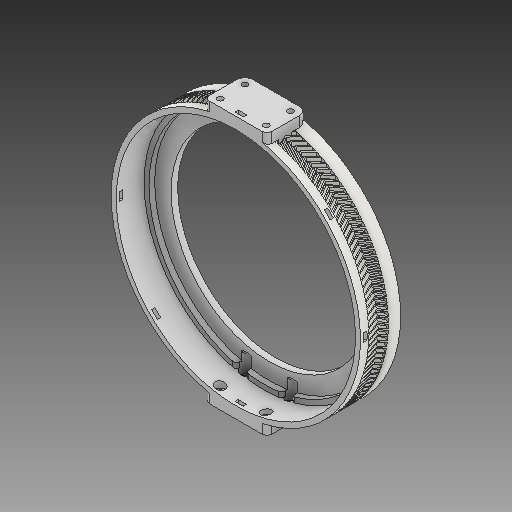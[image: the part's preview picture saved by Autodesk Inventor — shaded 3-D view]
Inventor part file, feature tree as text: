
AUTODESK INVENTOR PART (.ipt)
format: ipt  version: 2020 (Build 240168000, 168)  size: 2,971,648 bytes
history: native  units: in
note: dims shown in document units (in); Inventor stores cm internally (conversion verified against a paired STEP export)
features: other x5, extrude x5, sketch x5, plane x3, fillet x2, mirror x1
ambient origin geometry x8: Origin, YZ Plane, XZ Plane, XY Plane, X Axis, Y Axis, Z Axis, Center Point
bodies: Solid2 (feature_tree), Solid1 (feature_tree)
feature tree (21):
  other  "Blocks"
  extrude  "Extrusion1"  Depth=0.3937in
  extrude  "Extrusion3"  Depth=3.1496in
  plane  "Work Plane1"
  extrude  "Extrusion4"  Depth=0.4724in
  extrude  "Extrusion5"  Depth=1.1024in
  plane  "Work Plane2"
  extrude  "Extrusion6"  Depth=0.1181in TaperAngle=0.0deg
  fillet  "Fillet1"  [1 undecoded]
  mirror  "Mirror1"
  fillet  "Fillet2"  Radius=0.2362in
  sketch  "Sketch1"  dims[d0=0.0in d1=0.0in d5=0.3937in]
  sketch  "Sketch3"  dims[d6=0.1575in d7=0.0in d8=3.1496in]
  sketch  "Sketch4"  dims[d9=0.1575in d10=0.0in d11=0.4724in]
  other  "Block1"
  other  "Block2"
  sketch  "Sketch5"  dims[d12=0.5906in d13=1.1024in]
  sketch  "Sketch6"  dims[d14=0.1378in d15=0.6299in d16=0.0in d17=-0.1969in d18=0.2362in d19=0.3937in d20=0.0in d21=0.0787in d22=0.1181in]
  plane  "Work Plane3"
  other  "Block2:1"
  other  "Block1:2"
note: 1 required parameter value undecoded (feature->parameter linkage not recoverable at this tier; creation-order binding heuristic only, values carry confidence <= 0.55)
